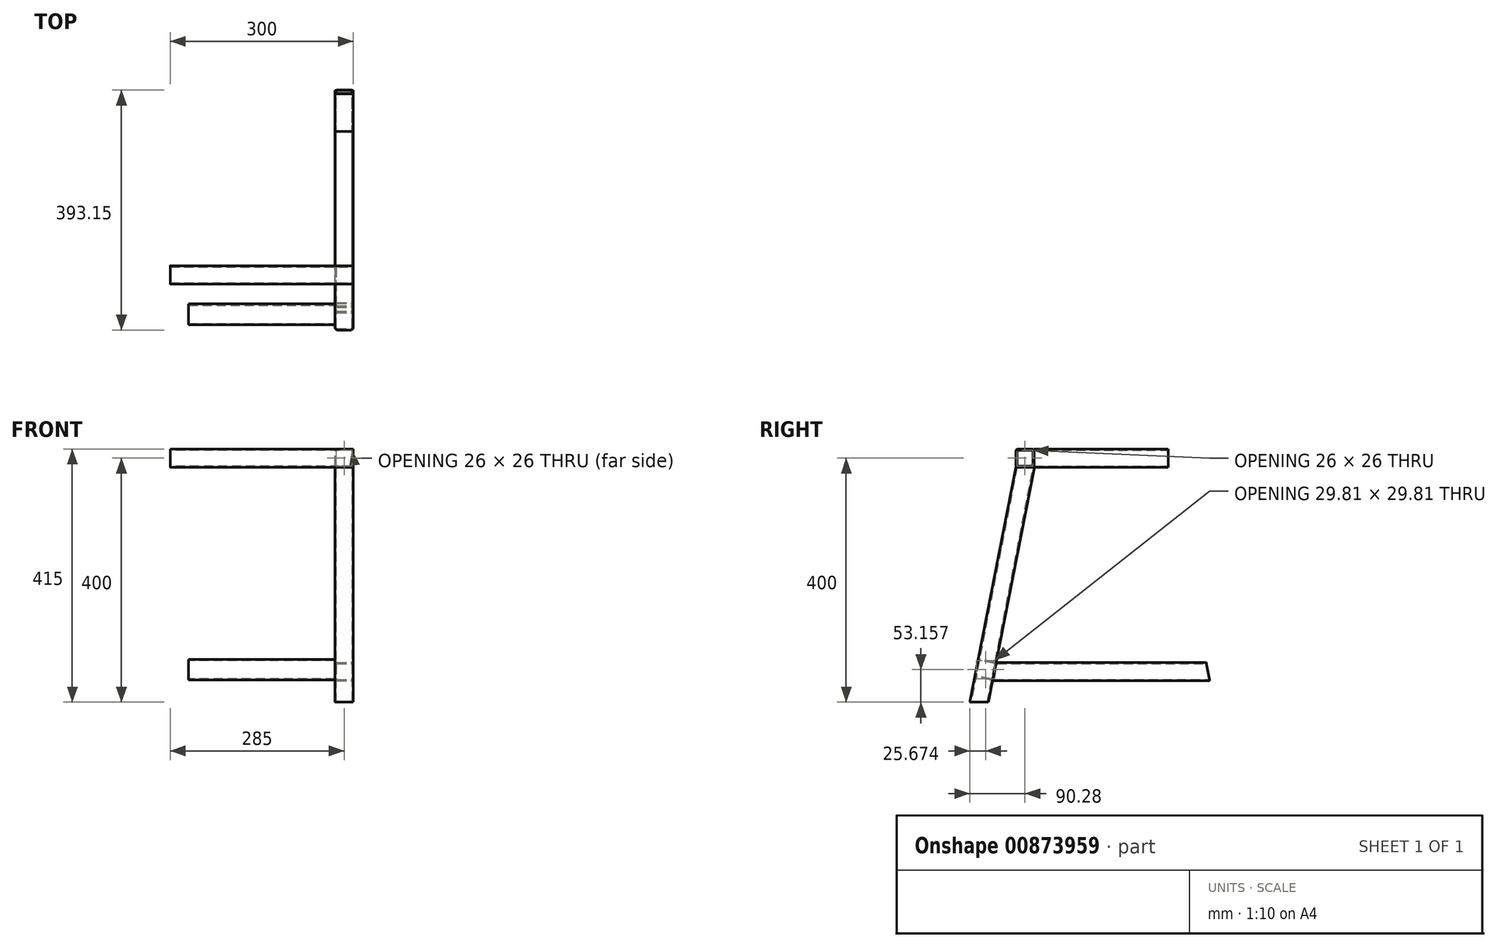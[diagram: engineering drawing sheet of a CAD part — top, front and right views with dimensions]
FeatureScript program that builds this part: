
annotation { "Feature Type Name" : "Feature", "Feature Type Description" : "" }
export const myFeature = defineFeature(function(context is Context, id is Id, definition is map)
    precondition{}
    {
        {
            var Q0;
            Q0=qCreatedBy(makeId("Top.planeOp"),FACE);
            cPlane(context, id + "F0", {"entities" : qUnion([Q0]), "cplaneType" : CPlaneType.OFFSET, "offset" : 50 * mm, "width" : 152.4 * mm, "height" : 152.4 * mm});
        }
        {
            var Q0;
            Q0=qCreatedBy(makeId("Top.planeOp"),FACE);
            cPlane(context, id + "F1", {"entities" : qUnion([Q0]), "cplaneType" : CPlaneType.OFFSET, "offset" : 400 * mm, "width" : 150 * mm, "height" : 150 * mm});
        }
        {
            var Q0;
            Q0=qCreatedBy(id+"F1.planeOp",FACE);
            var sketch = newSketch(context, id + "F2", { "sketchPlane" : qUnion([Q0])});
            skLineSegment(sketch, "E0.bottom", {"start": v(-150, 125) * mm, "end": v(150, 125) * mm});
            skLineSegment(sketch, "E0.top", {"start": v(-150, -125) * mm, "end": v(150, -125) * mm});
            skLineSegment(sketch, "E0.left", {"start": v(-150, 125) * mm, "end": v(-150, -125) * mm});
            skLineSegment(sketch, "E0.right", {"start": v(150, 125) * mm, "end": v(150, -125) * mm});
            skPoint(sketch, "E0.middle", {"position": v(0, 0) * mm});
            skSolve(sketch);
        }
        {
            var Q0;
            Q0=qCreatedBy(makeId("Right.planeOp"),FACE);
            var sketch = newSketch(context, id + "F3", { "sketchPlane" : qUnion([Q0])});
            skLineSegment(sketch, "E1.bottom", {"start": v(-110, 385) * mm, "end": v(-140, 385) * mm});
            skLineSegment(sketch, "E1.top", {"start": v(-110, 415) * mm, "end": v(-140, 415) * mm});
            skLineSegment(sketch, "E1.left", {"start": v(-110, 385) * mm, "end": v(-110, 415) * mm});
            skLineSegment(sketch, "E1.right", {"start": v(-140, 385) * mm, "end": v(-140, 415) * mm});
            skPoint(sketch, "E1.middle", {"position": v(-125, 400) * mm});
            skSolve(sketch);
        }
        {
            var Q0;
            Q0=makeQuery(id+"F3.imprint","IMPRINT",FACE,{"disambiguationData":[TD([[makeQuery(id+"F3.imprint","IMPRINT",EDGE,{"derivedFrom":sQuery(id+"F3.wireOp",EDGE,"E1.bottom")}),-1.0]])]});
            extrude(context, id + "F4", {"entities" : qUnion([Q0]), "depth" : 300 * mm, "offsetDistance" : 25 * mm, "symmetric" : true});
        }
        {
            var Q0;
            Q0=makeQuery(id+"F4.opExtrude","SWEPT_EDGE",EDGE,{"disambiguationData":[OSD([sQuery(id+"F3.wireOp",EDGE,"E1.top"),sQuery(id+"F3.wireOp",EDGE,"E1.right")])]});
            var Q1;
            Q1=makeQuery(id+"F4.opExtrude","SWEPT_EDGE",EDGE,{"disambiguationData":[OSD([sQuery(id+"F3.wireOp",EDGE,"E1.top"),sQuery(id+"F3.wireOp",EDGE,"E1.left")])]});
            var Q2;
            Q2=makeQuery(id+"F4.opExtrude","SWEPT_EDGE",EDGE,{"disambiguationData":[OSD([sQuery(id+"F3.wireOp",EDGE,"E1.bottom"),sQuery(id+"F3.wireOp",EDGE,"E1.right")])]});
            var Q3;
            Q3=makeQuery(id+"F4.opExtrude","SWEPT_EDGE",EDGE,{"disambiguationData":[OSD([sQuery(id+"F3.wireOp",EDGE,"E1.bottom"),sQuery(id+"F3.wireOp",EDGE,"E1.left")])]});
            fillet(context, id + "F5", {"entities" : qUnion([Q0, Q1, Q2, Q3]), "radius" : 4 * mm, "tangentPropagation" : true, "allowEdgeOverflow" : false});
        }
        {
            var Q0;
            Q0=makeQuery(id+"F4.opExtrude","CAP_FACE",FACE,{"disambiguationData":[OSD([sQuery(id+"F3.wireOp",EDGE,"E1.bottom"),sQuery(id+"F3.wireOp",EDGE,"E1.top"),sQuery(id+"F3.wireOp",EDGE,"E1.left"),sQuery(id+"F3.wireOp",EDGE,"E1.right")])],"isStart":false});
            var Q1;
            Q1=makeQuery(id+"F4.opExtrude","CAP_FACE",FACE,{"disambiguationData":[OSD([sQuery(id+"F3.wireOp",EDGE,"E1.bottom"),sQuery(id+"F3.wireOp",EDGE,"E1.top"),sQuery(id+"F3.wireOp",EDGE,"E1.left"),sQuery(id+"F3.wireOp",EDGE,"E1.right")])],"isStart":true});
            shell(context, id + "F6", {"entities" : qUnion([Q0, Q1]), "thickness" : 2 * mm});
        }
        {
            var Q0;
            Q0=qCreatedBy(makeId("Front.planeOp"),FACE);
            var sketch = newSketch(context, id + "F7", { "sketchPlane" : qUnion([Q0])});
            skLineSegment(sketch, "E2.bottom", {"start": v(150, 385) * mm, "end": v(120, 385) * mm});
            skLineSegment(sketch, "E2.top", {"start": v(150, 415) * mm, "end": v(120, 415) * mm});
            skLineSegment(sketch, "E2.left", {"start": v(150, 385) * mm, "end": v(150, 415) * mm});
            skLineSegment(sketch, "E2.right", {"start": v(120, 385) * mm, "end": v(120, 415) * mm});
            skPoint(sketch, "E2.middle", {"position": v(135, 400) * mm});
            skPoint(sketch, "E3", {"position": v(150, 400) * mm});
            skSolve(sketch);
        }
        {
            var Q0;
            Q0=makeQuery(id+"F7.imprint","IMPRINT",FACE,{"disambiguationData":[TD([[makeQuery(id+"F7.imprint","IMPRINT",EDGE,{"derivedFrom":sQuery(id+"F7.wireOp",EDGE,"E2.bottom")}),-1.0]])]});
            extrude(context, id + "F8", {"entities" : qUnion([Q0]), "depth" : 220 * mm, "offsetDistance" : 25 * mm, "symmetric" : true});
        }
        {
            var Q0;
            Q0=makeQuery(id+"F8.opExtrude","SWEPT_EDGE",EDGE,{"disambiguationData":[OSD([sQuery(id+"F7.wireOp",EDGE,"E2.top"),sQuery(id+"F7.wireOp",EDGE,"E2.left")])]});
            var Q1;
            Q1=makeQuery(id+"F8.opExtrude","SWEPT_EDGE",EDGE,{"disambiguationData":[OSD([sQuery(id+"F7.wireOp",EDGE,"E2.top"),sQuery(id+"F7.wireOp",EDGE,"E2.right")])]});
            var Q2;
            Q2=makeQuery(id+"F8.opExtrude","SWEPT_EDGE",EDGE,{"disambiguationData":[OSD([sQuery(id+"F7.wireOp",EDGE,"E2.bottom"),sQuery(id+"F7.wireOp",EDGE,"E2.left")])]});
            var Q3;
            Q3=makeQuery(id+"F8.opExtrude","SWEPT_EDGE",EDGE,{"disambiguationData":[OSD([sQuery(id+"F7.wireOp",EDGE,"E2.bottom"),sQuery(id+"F7.wireOp",EDGE,"E2.right")])]});
            fillet(context, id + "F9", {"entities" : qUnion([Q0, Q1, Q2, Q3]), "radius" : 4 * mm, "tangentPropagation" : true, "allowEdgeOverflow" : false});
        }
        {
            var Q0;
            Q0=makeQuery(id+"F8.opExtrude","CAP_FACE",FACE,{"disambiguationData":[OSD([sQuery(id+"F7.wireOp",EDGE,"E2.bottom"),sQuery(id+"F7.wireOp",EDGE,"E2.top"),sQuery(id+"F7.wireOp",EDGE,"E2.left"),sQuery(id+"F7.wireOp",EDGE,"E2.right")])],"isStart":true});
            var Q1;
            Q1=makeQuery(id+"F8.opExtrude","CAP_FACE",FACE,{"disambiguationData":[OSD([sQuery(id+"F7.wireOp",EDGE,"E2.bottom"),sQuery(id+"F7.wireOp",EDGE,"E2.top"),sQuery(id+"F7.wireOp",EDGE,"E2.left"),sQuery(id+"F7.wireOp",EDGE,"E2.right")])],"isStart":false});
            shell(context, id + "F10", {"entities" : qUnion([Q0, Q1]), "thickness" : 2 * mm});
        }
        {
            var Q0;
            Q0=makeQuery(id+"F8.opExtrude","SWEPT_FACE",FACE,{"disambiguationData":[OSD([sQuery(id+"F7.wireOp",EDGE,"E2.left")])]});
            var sketch = newSketch(context, id + "F11", { "sketchPlane" : qUnion([Q0])});
            skLineSegment(sketch, "E4", {"start": v(-140, 385) * mm, "end": v(-215.28, 0) * mm});
            skLineSegment(sketch, "E5", {"start": v(-215.28, 0) * mm, "end": v(-184.72, 0) * mm});
            skLineSegment(sketch, "E6", {"start": v(-184.72, 0) * mm, "end": v(-109.43, 385) * mm});
            skLineSegment(sketch, "E7", {"start": v(-109.43, 385) * mm, "end": v(-140, 385) * mm});
            skPoint(sketch, "E8", {"position": v(-200, 0) * mm});
            skLineSegment(sketch, "E9", {"start": v(0, 0) * mm, "end": v(0, 385) * mm, "construction": true});
            skLineSegment(sketch, "E10", {"start": v(177.87, 35) * mm, "end": v(-177.87, 35) * mm});
            skLineSegment(sketch, "E11", {"start": v(-177.87, 35) * mm, "end": v(-172, 65) * mm});
            skLineSegment(sketch, "E12", {"start": v(-172, 65) * mm, "end": v(172, 65) * mm});
            skLineSegment(sketch, "E13", {"start": v(172, 65) * mm, "end": v(177.87, 35) * mm});
            skLineSegment(sketch, "E14", {"start": v(-174.94, 50) * mm, "end": v(174.94, 50) * mm, "construction": true});
            skSolve(sketch);
        }
        {
            var Q0;
            {var subQ3=sQuery(id+"F11.wireOp",EDGE,"E4");Q0=makeQuery(id+"F11.imprint","IMPRINT",FACE,{"disambiguationData":[TD([[makeQuery(id+"F11.imprint","IMPRINT",EDGE,{"derivedFrom":subQ3}),1.0]])]});}
            extrude(context, id + "F12", {"entities" : qUnion([Q0]), "oppositeDirection" : true, "depth" : 30 * mm, "offsetDistance" : 25 * mm});
        }
        {
            var Q0;
            Q0=makeQuery(id+"F12.opExtrude","CAP_EDGE",EDGE,{"disambiguationData":[OSD([sQuery(id+"F11.wireOp",EDGE,"E4")])],"isStart":true});
            var Q1;
            Q1=makeQuery(id+"F12.opExtrude","CAP_EDGE",EDGE,{"disambiguationData":[OSD([sQuery(id+"F11.wireOp",EDGE,"E6"),sQuery(id+"F11.wireOp",EDGE,"E11")])],"isStart":true});
            var Q2;
            Q2=makeQuery(id+"F12.opExtrude","CAP_EDGE",EDGE,{"disambiguationData":[OSD([sQuery(id+"F11.wireOp",EDGE,"E4")])],"isStart":false});
            var Q3;
            Q3=makeQuery(id+"F12.opExtrude","CAP_EDGE",EDGE,{"disambiguationData":[OSD([sQuery(id+"F11.wireOp",EDGE,"E6"),sQuery(id+"F11.wireOp",EDGE,"E11")])],"isStart":false});
            fillet(context, id + "F13", {"entities" : qUnion([Q0, Q1, Q2, Q3]), "radius" : 4 * mm, "tangentPropagation" : true, "allowEdgeOverflow" : false});
        }
        {
            var Q0;
            Q0=makeQuery(id+"F12.opExtrude","SWEPT_FACE",FACE,{"disambiguationData":[OSD([sQuery(id+"F11.wireOp",EDGE,"E7")])]});
            var Q1;
            Q1=makeQuery(id+"F12.opExtrude","SWEPT_FACE",FACE,{"disambiguationData":[OSD([sQuery(id+"F11.wireOp",EDGE,"E5")])]});
            shell(context, id + "F14", {"entities" : qUnion([Q0, Q1]), "thickness" : 2 * mm});
        }
        {
            var Q0;
            Q0=makeQuery(id+"F11.imprint","IMPRINT",FACE,{"disambiguationData":[TD([[makeQuery(id+"F11.imprint","IMPRINT",EDGE,{"derivedFrom":sQuery(id+"F11.wireOp",EDGE,"E10")}),-1.0]])]});
            extrude(context, id + "F15", {"entities" : qUnion([Q0]), "oppositeDirection" : true, "depth" : 30 * mm, "offsetDistance" : 25 * mm});
        }
        {
            var Q0;
            Q0=makeQuery(id+"F15.opExtrude","CAP_EDGE",EDGE,{"disambiguationData":[OSD([sQuery(id+"F11.wireOp",EDGE,"E12")])],"isStart":true});
            var Q1;
            Q1=makeQuery(id+"F15.opExtrude","CAP_EDGE",EDGE,{"disambiguationData":[OSD([sQuery(id+"F11.wireOp",EDGE,"E12")])],"isStart":false});
            var Q2;
            Q2=makeQuery(id+"F15.opExtrude","CAP_EDGE",EDGE,{"disambiguationData":[OSD([sQuery(id+"F11.wireOp",EDGE,"E10")])],"isStart":true});
            var Q3;
            Q3=makeQuery(id+"F15.opExtrude","CAP_EDGE",EDGE,{"disambiguationData":[OSD([sQuery(id+"F11.wireOp",EDGE,"E10")])],"isStart":false});
            fillet(context, id + "F16", {"entities" : qUnion([Q0, Q1, Q2, Q3]), "radius" : 4 * mm, "tangentPropagation" : true, "allowEdgeOverflow" : false});
        }
        {
            var Q0;
            Q0=makeQuery(id+"F15.opExtrude","SWEPT_FACE",FACE,{"disambiguationData":[OSD([sQuery(id+"F11.wireOp",EDGE,"E11")])]});
            var Q1;
            Q1=makeQuery(id+"F15.opExtrude","SWEPT_FACE",FACE,{"disambiguationData":[OSD([sQuery(id+"F11.wireOp",EDGE,"E13")])]});
            shell(context, id + "F17", {"entities" : qUnion([Q0, Q1]), "thickness" : 2 * mm});
        }
        {
            var Q0;
            Q0=makeQuery(id+"F12.opExtrude","SWEPT_FACE",FACE,{"disambiguationData":[OSD([sQuery(id+"F11.wireOp",EDGE,"E4")])]});
            var sketch = newSketch(context, id + "F18", { "sketchPlane" : qUnion([Q0])});
            skLineSegment(sketch, "E15", {"start": v(0, 0) * mm, "end": v(0, 308.54) * mm, "construction": true});
            skLineSegment(sketch, "E16.bottom", {"start": v(120, 30.78) * mm, "end": v(-120, 30.78) * mm});
            skLineSegment(sketch, "E16.top", {"start": v(120, 0.78) * mm, "end": v(-120, 0.78) * mm});
            skLineSegment(sketch, "E16.left", {"start": v(120, 30.78) * mm, "end": v(120, 0.78) * mm});
            skLineSegment(sketch, "E16.right", {"start": v(-120, 30.78) * mm, "end": v(-120, 0.78) * mm});
            skPoint(sketch, "E16.middle", {"position": v(0, 15.78) * mm});
            skSolve(sketch);
        }
        {
            var Q0;
            Q0 = qSketchRegion(id + "F18", true);
            extrude(context, id + "F19", {"entities" : qUnion([Q0]), "oppositeDirection" : true, "depth" : 30 * mm, "offsetDistance" : 25 * mm});
        }
        {
            var Q0;
            Q0=makeQuery(id+"F19.opExtrude","CAP_EDGE",EDGE,{"disambiguationData":[OSD([sQuery(id+"F18.wireOp",EDGE,"E16.bottom")])],"isStart":true});
            var Q1;
            Q1=makeQuery(id+"F19.opExtrude","CAP_EDGE",EDGE,{"disambiguationData":[OSD([sQuery(id+"F18.wireOp",EDGE,"E16.top")])],"isStart":true});
            var Q2;
            Q2=makeQuery(id+"F19.opExtrude","CAP_EDGE",EDGE,{"disambiguationData":[OSD([sQuery(id+"F18.wireOp",EDGE,"E16.top")])],"isStart":false});
            var Q3;
            Q3=makeQuery(id+"F19.opExtrude","CAP_EDGE",EDGE,{"disambiguationData":[OSD([sQuery(id+"F18.wireOp",EDGE,"E16.bottom")])],"isStart":false});
            fillet(context, id + "F20", {"entities" : qUnion([Q0, Q1, Q2, Q3]), "radius" : 4 * mm, "tangentPropagation" : true, "allowEdgeOverflow" : false});
        }
        {
            var Q0;
            Q0=makeQuery(id+"F19.opExtrude","SWEPT_FACE",FACE,{"disambiguationData":[OSD([sQuery(id+"F18.wireOp",EDGE,"E16.right")])]});
            var Q1;
            Q1=makeQuery(id+"F19.opExtrude","SWEPT_FACE",FACE,{"disambiguationData":[OSD([sQuery(id+"F18.wireOp",EDGE,"E16.left")])]});
            shell(context, id + "F21", {"entities" : qUnion([Q0, Q1]), "thickness" : 2 * mm});
        }
    });
